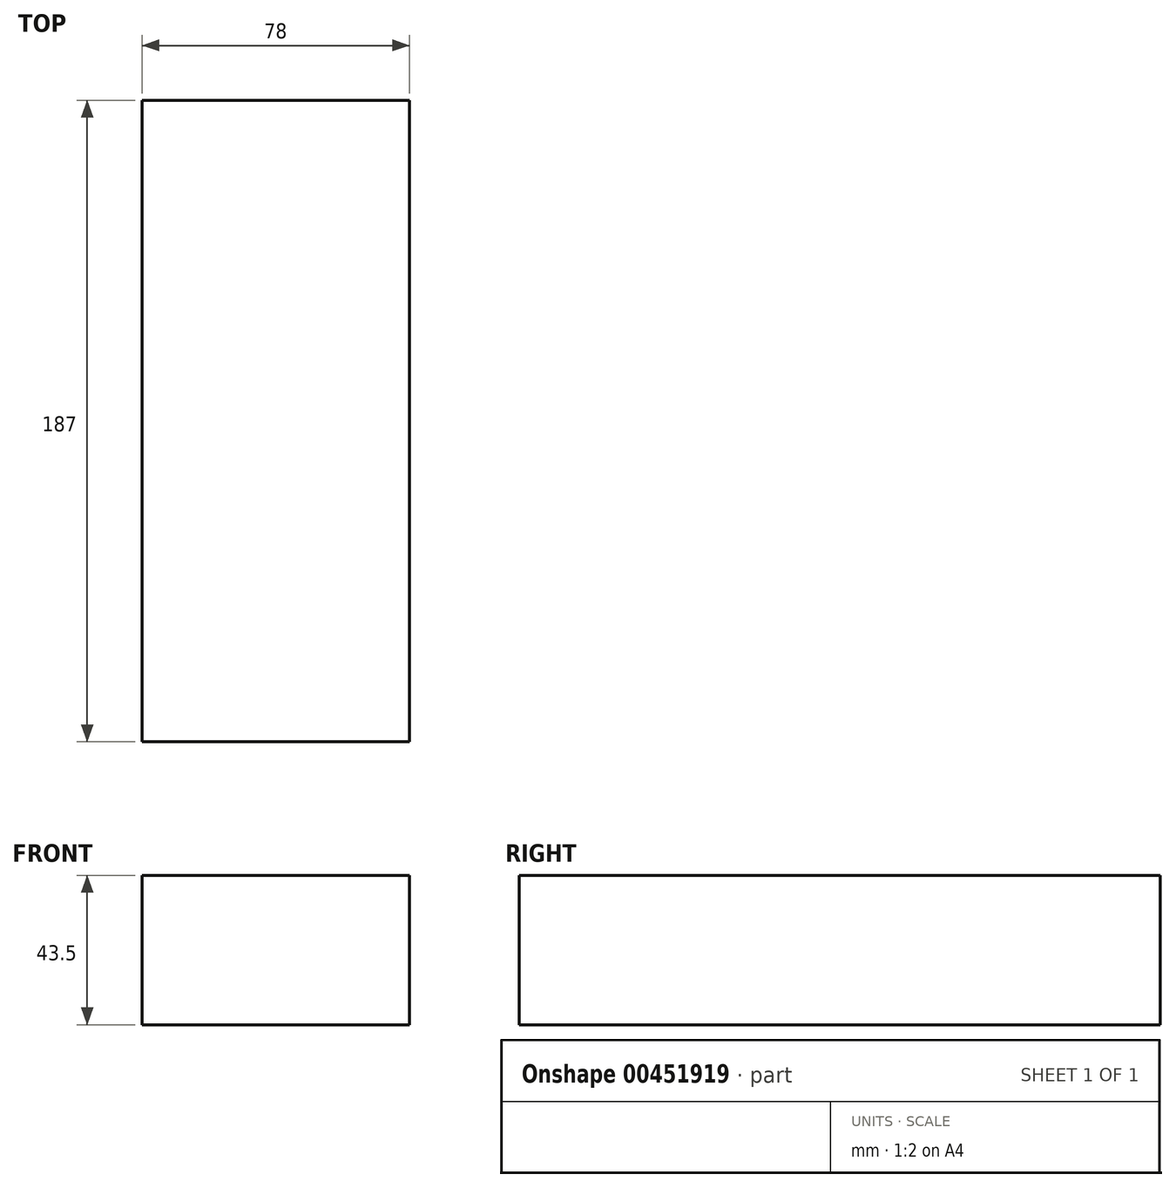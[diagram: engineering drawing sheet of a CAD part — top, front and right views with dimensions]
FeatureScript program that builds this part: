
annotation { "Feature Type Name" : "Feature", "Feature Type Description" : "" }
export const myFeature = defineFeature(function(context is Context, id is Id, definition is map)
    precondition{}
    {
        {
            var Q0;
            Q0=qCreatedBy(makeId("Right.planeOp"),FACE);
            var sketch = newSketch(context, id + "F0", { "sketchPlane" : qUnion([Q0])});
            skLineSegment(sketch, "E0.bottom", {"start": v(0, 0) * mm, "end": v(-187, 0) * mm});
            skLineSegment(sketch, "E0.top", {"start": v(0, 43.5) * mm, "end": v(-187, 43.5) * mm});
            skLineSegment(sketch, "E0.left", {"start": v(0, 0) * mm, "end": v(0, 43.5) * mm});
            skLineSegment(sketch, "E0.right", {"start": v(-187, 0) * mm, "end": v(-187, 43.5) * mm});
            skSolve(sketch);
        }
        {
            var Q0;
            Q0=makeQuery(id+"F0.imprint","IMPRINT",FACE,{"disambiguationData":[TD([[makeQuery(id+"F0.imprint","IMPRINT",EDGE,{"derivedFrom":sQuery(id+"F0.wireOp",EDGE,"E0.bottom")}),-1.0]])]});
            extrude(context, id + "F1", {"entities" : qUnion([Q0]), "depth" : 78 * mm});
        }
    });
